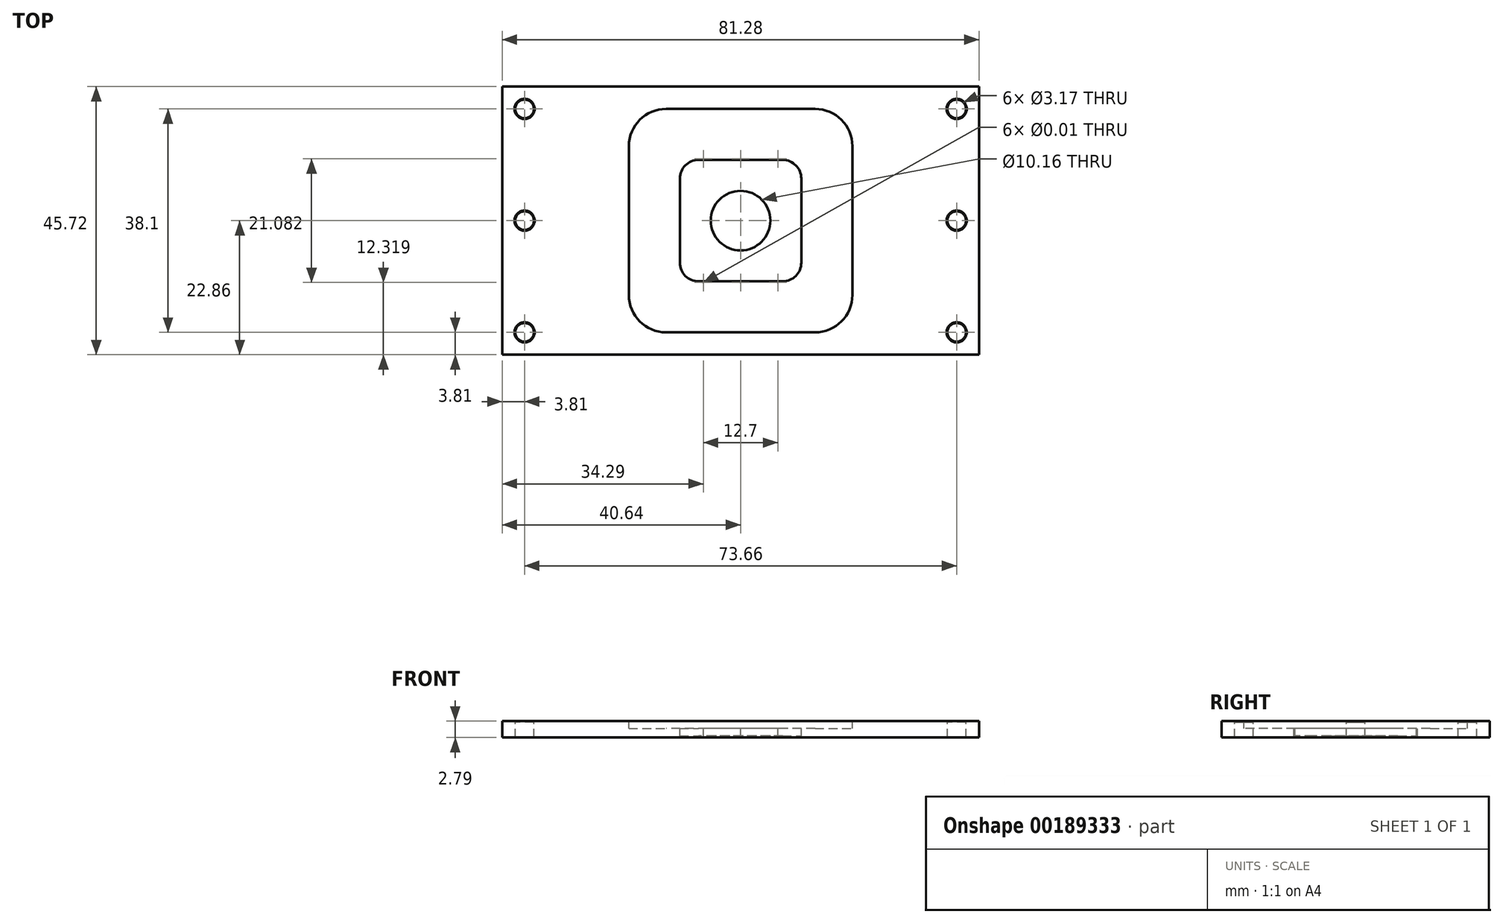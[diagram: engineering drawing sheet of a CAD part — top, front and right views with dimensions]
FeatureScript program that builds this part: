
annotation { "Feature Type Name" : "Feature", "Feature Type Description" : "" }
export const myFeature = defineFeature(function(context is Context, id is Id, definition is map)
    precondition{}
    {
        {
            var Q0;
            Q0=qCreatedBy(makeId("Top.planeOp"),FACE);
            var sketch = newSketch(context, id + "F0", { "sketchPlane" : qUnion([Q0])});
            skLineSegment(sketch, "E0.bottom", {"start": v(40.64, 22.86) * mm, "end": v(-40.64, 22.86) * mm});
            skLineSegment(sketch, "E0.top", {"start": v(40.64, -22.86) * mm, "end": v(-40.64, -22.86) * mm});
            skLineSegment(sketch, "E0.left", {"start": v(40.64, 22.86) * mm, "end": v(40.64, -22.86) * mm});
            skLineSegment(sketch, "E0.right", {"start": v(-40.64, 22.86) * mm, "end": v(-40.64, -22.86) * mm});
            skPoint(sketch, "E0.middle", {"position": v(0, 0) * mm});
            skSolve(sketch);
        }
        {
            var Q0;
            Q0=makeQuery(id+"F0.imprint","IMPRINT",FACE,{"disambiguationData":[TD([[makeQuery(id+"F0.imprint","IMPRINT",EDGE,{"derivedFrom":sQuery(id+"F0.wireOp",EDGE,"E0.bottom")}),1.0]])]});
            extrude(context, id + "F1", {"entities" : qUnion([Q0]), "depth" : 2.8 * mm});
        }
        {
            var Q0;
            Q0=makeQuery(id+"F1.opExtrude","CAP_FACE",FACE,{"disambiguationData":[OSD([sQuery(id+"F0.wireOp",EDGE,"E0.bottom"),sQuery(id+"F0.wireOp",EDGE,"E0.top"),sQuery(id+"F0.wireOp",EDGE,"E0.left"),sQuery(id+"F0.wireOp",EDGE,"E0.right")])],"isStart":false});
            var sketch = newSketch(context, id + "F2", { "sketchPlane" : qUnion([Q0])});
            skLineSegment(sketch, "E1.bottom", {"start": v(12.7, 19.05) * mm, "end": v(-12.7, 19.05) * mm});
            skLineSegment(sketch, "E1.top", {"start": v(12.7, -19.05) * mm, "end": v(-12.7, -19.05) * mm});
            skLineSegment(sketch, "E1.left", {"start": v(19.05, 12.7) * mm, "end": v(19.05, -12.7) * mm});
            skLineSegment(sketch, "E1.right", {"start": v(-19.05, 12.7) * mm, "end": v(-19.05, -12.7) * mm});
            skPoint(sketch, "E1.middle", {"position": v(0, 0) * mm});
            skLineSegment(sketch, "E2.bottom", {"start": v(7.18, 10.35) * mm, "end": v(-7.18, 10.35) * mm});
            skLineSegment(sketch, "E2.top", {"start": v(7.18, -10.35) * mm, "end": v(-7.18, -10.35) * mm});
            skLineSegment(sketch, "E2.left", {"start": v(10.35, 7.18) * mm, "end": v(10.35, -7.18) * mm});
            skLineSegment(sketch, "E2.right", {"start": v(-10.35, 7.18) * mm, "end": v(-10.35, -7.18) * mm});
            skCircle(sketch, "E3", {"center": v(0, 0) * mm, "radius": 5.08 * mm});
            skPoint(sketch, "E4.visualSharp", {"position": v(-19.05, 19.05) * mm});
            skArc(sketch, "E4.filletArc", {"start": v(-12.7, 19.05) * mm, "mid": v(-17.2, 17.2) * mm, "end": v(-19.05, 12.7) * mm});
            skPoint(sketch, "E5.visualSharp", {"position": v(-19.05, -19.05) * mm});
            skArc(sketch, "E5.filletArc", {"start": v(-19.05, -12.7) * mm, "mid": v(-17.2, -17.2) * mm, "end": v(-12.7, -19.05) * mm});
            skPoint(sketch, "E6.visualSharp", {"position": v(19.05, -19.05) * mm});
            skArc(sketch, "E6.filletArc", {"start": v(12.7, -19.05) * mm, "mid": v(17.2, -17.2) * mm, "end": v(19.05, -12.7) * mm});
            skPoint(sketch, "E7.visualSharp", {"position": v(19.05, 19.05) * mm});
            skArc(sketch, "E7.filletArc", {"start": v(19.05, 12.7) * mm, "mid": v(17.2, 17.2) * mm, "end": v(12.7, 19.05) * mm});
            skPoint(sketch, "E8.visualSharp", {"position": v(-10.35, 10.35) * mm});
            skArc(sketch, "E8.filletArc", {"start": v(-7.18, 10.35) * mm, "mid": v(-9.42, 9.42) * mm, "end": v(-10.35, 7.18) * mm});
            skPoint(sketch, "E9.visualSharp", {"position": v(-10.35, -10.35) * mm});
            skArc(sketch, "E9.filletArc", {"start": v(-10.35, -7.18) * mm, "mid": v(-9.42, -9.42) * mm, "end": v(-7.18, -10.35) * mm});
            skPoint(sketch, "E10.visualSharp", {"position": v(10.35, -10.35) * mm});
            skArc(sketch, "E10.filletArc", {"start": v(7.18, -10.35) * mm, "mid": v(9.42, -9.42) * mm, "end": v(10.35, -7.18) * mm});
            skPoint(sketch, "E11.visualSharp", {"position": v(10.35, 10.35) * mm});
            skArc(sketch, "E11.filletArc", {"start": v(10.35, 7.18) * mm, "mid": v(9.42, 9.42) * mm, "end": v(7.18, 10.35) * mm});
            skLineSegment(sketch, "E12", {"start": v(-36.83, -19.05) * mm, "end": v(-36.83, 19.05) * mm});
            skLineSegment(sketch, "E13", {"start": v(36.83, -19.05) * mm, "end": v(36.83, 19.05) * mm});
            skPoint(sketch, "E14", {"position": v(-36.83, 0) * mm});
            skPoint(sketch, "E15", {"position": v(36.83, 0) * mm});
            skSolve(sketch);
        }
        {
            var Q0;
            Q0=makeQuery(id+"F2.imprint","IMPRINT",FACE,{"disambiguationData":[TD([[makeQuery(id+"F2.imprint","IMPRINT",EDGE,{"derivedFrom":sQuery(id+"F2.wireOp",EDGE,"E1.bottom")}),1.0]])]});
            extrude(context, id + "F3", {"entities" : qUnion([Q0]), "operationType" : NewBodyOperationType.REMOVE, "oppositeDirection" : true, "depth" : 1.27 * mm});
        }
        {
            var Q0;
            Q0=makeQuery(id+"F3.boolean.opBoolean","SPLIT",FACE,{"disambiguationData":[TD([makeQuery(id+"F3.opExtrude","SWEPT_FACE",FACE,{"disambiguationData":[OSD([sQuery(id+"F2.wireOp",EDGE,"E2.bottom")])]})])],"derivedFrom":makeQuery(id+"F1.opExtrude","CAP_FACE",FACE,{"disambiguationData":[OSD([sQuery(id+"F0.wireOp",EDGE,"E0.bottom"),sQuery(id+"F0.wireOp",EDGE,"E0.top"),sQuery(id+"F0.wireOp",EDGE,"E0.left"),sQuery(id+"F0.wireOp",EDGE,"E0.right")])],"isStart":false})});
            extrude(context, id + "F4", {"entities" : qUnion([Q0]), "operationType" : NewBodyOperationType.REMOVE, "oppositeDirection" : true, "depth" : 2.54 * mm});
        }
        {
            var Q0;
            Q0=makeQuery(id+"F2.imprint","IMPRINT",FACE,{"disambiguationData":[TD([[makeQuery(id+"F2.imprint","IMPRINT",EDGE,{"derivedFrom":sQuery(id+"F2.wireOp",EDGE,"E3")}),1.0]])]});
            extrude(context, id + "F5", {"entities" : qUnion([Q0]), "operationType" : NewBodyOperationType.REMOVE, "endBound" : BoundingType.THROUGH_ALL, "oppositeDirection" : true, "depth" : 25.4 * mm});
        }
        {
            var Q0;
            Q0=sQuery(id+"F2.wireOp",VERTEX,"E12.end");
            var Q1;
            Q1=sQuery(id+"F2.wireOp",VERTEX,"E12.start");
            var Q2;
            Q2=sQuery(id+"F2.wireOp",VERTEX,"E13.start");
            var Q3;
            Q3=sQuery(id+"F2.wireOp",VERTEX,"E13.end");
            var Q4;
            Q4=sQuery(id+"F2.wireOp",VERTEX,"E14");
            var Q5;
            Q5=sQuery(id+"F2.wireOp",VERTEX,"E15");
            var Q6;
            Q6=makeQuery(id+"F1.opExtrude","SWEPT_BODY",BODY,{"disambiguationData":[OSD([sQuery(id+"F0.wireOp",EDGE,"E0.bottom"),sQuery(id+"F0.wireOp",EDGE,"E0.top"),sQuery(id+"F0.wireOp",EDGE,"E0.left"),sQuery(id+"F0.wireOp",EDGE,"E0.right")])]});
            hole(context, id + "F6", {"style" : HoleStyle.C_SINK, "endStyle" : HoleEndStyle.THROUGH, "holeDiameter" : 3.17 * mm, "cSinkDiameter" : 3.43 * mm, "cSinkAngle" : 82 * degree, "locations" : qUnion([Q0, Q1, Q2, Q3, Q4, Q5]), "scope" : qUnion([Q6]), "isTappedThrough" : true});
        }
        {
            var Q0;
            Q0=makeQuery(id+"F2.imprint","IMPRINT",FACE,{"disambiguationData":[TD([[makeQuery(id+"F2.imprint","IMPRINT",EDGE,{"derivedFrom":sQuery(id+"F2.wireOp",EDGE,"E1.bottom")}),1.0]])]});
            var sketch = newSketch(context, id + "F7", { "sketchPlane" : qUnion([Q0])});
            skPoint(sketch, "E16", {"position": v(-6.35, 10.54) * mm});
            skPoint(sketch, "E17.0.1.0", {"position": v(-6.35, -10.54) * mm});
            skPoint(sketch, "E17.1.0.0", {"position": v(0, 10.54) * mm});
            skPoint(sketch, "E17.1.1.0", {"position": v(0, -10.54) * mm});
            skPoint(sketch, "E17.2.0.0", {"position": v(6.35, 10.54) * mm});
            skPoint(sketch, "E17.2.1.0", {"position": v(6.35, -10.54) * mm});
            skLineSegment(sketch, "E17.direction1", {"start": v(-6.35, 10.54) * mm, "end": v(0, 10.54) * mm, "construction": true});
            skLineSegment(sketch, "E17.direction2", {"start": v(-6.35, 10.54) * mm, "end": v(-6.35, -10.54) * mm, "construction": true});
            skSolve(sketch);
        }
        {
            var Q0;
            Q0=sQuery(id+"F7.wireOp",VERTEX,"E16");
            var Q1;
            Q1=sQuery(id+"F7.wireOp",VERTEX,"E17.1.0.0");
            var Q2;
            Q2=sQuery(id+"F7.wireOp",VERTEX,"E17.2.0.0");
            var Q3;
            Q3=sQuery(id+"F7.wireOp",VERTEX,"E17.2.1.0");
            var Q4;
            Q4=sQuery(id+"F7.wireOp",VERTEX,"E17.1.1.0");
            var Q5;
            Q5=sQuery(id+"F7.wireOp",VERTEX,"E17.0.1.0");
            var Q6;
            Q6=makeQuery(id+"F1.opExtrude","SWEPT_BODY",BODY,{"disambiguationData":[OSD([sQuery(id+"F0.wireOp",EDGE,"E0.bottom"),sQuery(id+"F0.wireOp",EDGE,"E0.top"),sQuery(id+"F0.wireOp",EDGE,"E0.left"),sQuery(id+"F0.wireOp",EDGE,"E0.right")])]});
            hole(context, id + "F8", {"style" : HoleStyle.SIMPLE, "endStyle" : HoleEndStyle.BLIND, "holeDiameter" : 0.01 * mm, "holeDepth" : 7.62 * mm, "locations" : qUnion([Q0, Q1, Q2, Q3, Q4, Q5]), "scope" : qUnion([Q6])});
        }
    });
